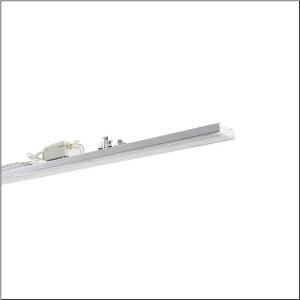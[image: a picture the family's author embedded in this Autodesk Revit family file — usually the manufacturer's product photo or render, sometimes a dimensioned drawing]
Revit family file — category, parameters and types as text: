
# Revit family: licross_r__21_recessed_ho_52te12dv4l2m3s_586b
name_source: partatom
category: Lighting Fixtures
units: mm (PartAtom-declared; Revit-internal decimal feet)

## family parameters
Cut with Voids When Loaded = No
Host = Face
Light Source = No
Part Type = Normal
Room Calculation Point = No
Round Connector Dimension = Use Diameter
Shared = No

## types (1)
- --- (1 x LED, 910 lm, 6.4 W, 4000K)
    Apparent Load = 6 VA
    CIE Flux Codes = 69 91 98 100 100
    Color Rendering = 80
    Color Temperature = 4000K
    Default Elevation = 1800 mm
    Description = Licross® 21 Recessed HO, luminaire insert, of sheet steel, galvanised, coil coated, white, length: 2.250mm, width: 66mm, height: 67mm, LED rated luminous flux: 22.710lm, light colour: 840, control gear: DALI 2, with plug, 6-pole, with phase selection, for trunking rail, 14-core, mains connection: 220..240V, AC, 50/60Hz, rated input power: 129W, for trunking rail, 14-core, halogen-free wiring, for emergency light function, converter,control gear: single battery element, battery: LiFeP04, 9Ah, primary optical cover: cover, of PMMA, light emission: direct distribution, primary light characteristic: symmetric, protection rating (complete): IP54, insulation class (complete): insulation class I (protective earthing), certification: CE, UKCA, protection symbol: D if used in an environment with non-conductive dust loads with corresponding accessories, impact resistance: IK06, permissible ambient temperature for indoor applications: +5..+30°C, standard: EN 60598-2-22, LABS conformity tested according to VDMA 24364:2018-05, reducing of maximum allowable ambient temperature of 5°C with ceiling mounting, corresponds to IFS (International Featured Standards) requirements for safety and quality in the food industry, packaging unit: 1 piece
    Height = 58 mm
    Lamp = 1 x LED
    Lamp Light Flux = 910 lm
    Lamp Power = 6.4 W
    Lamp count = 1
    Length = 2250 mm
    Luminous efficacy = 142 lm/W
    Manufacturer = Siteco
    ModVariant = No
    Model = 52TE12DV4L2M3S
    Mounting Place = Ceiling
    Mounting Type = Pendant
    Number of Poles = 1
    OnlyDefault = Yes
    Power Factor = 1
    Product Name = Licross® 21 Recessed HO
    Product group = luminaire insert
    ProductGroupID = 901
    Protection Class = Protection class I
    Protection Degree = IP 54
    RLX_Detail_Level = 1
    RLX_Emergency_Light_Flux = 0 lm
    RLX_Emergency_Type = 0
    RLX_Emergency_Type_DB = No
    RlxData = <blob elided: 29973 chars, md5=16a59eb1>
    Socket = socket
    Standby Power = 0 W
    System Light Flux = 910 lm
    System Power = 6 W
    Type Comments = : emergency light operation: 3 h
    Type Image = l_1296930.jpg
    URL = http://relux.com
    VarID = @adj_039461
    Voltage = 0 V
    Weight = 0.00 kg
    Width = 66 mm

## geometry (parser evidence)
native form markers: Blend x4, Sweep x8
no freeform markers — native parametric forms only
